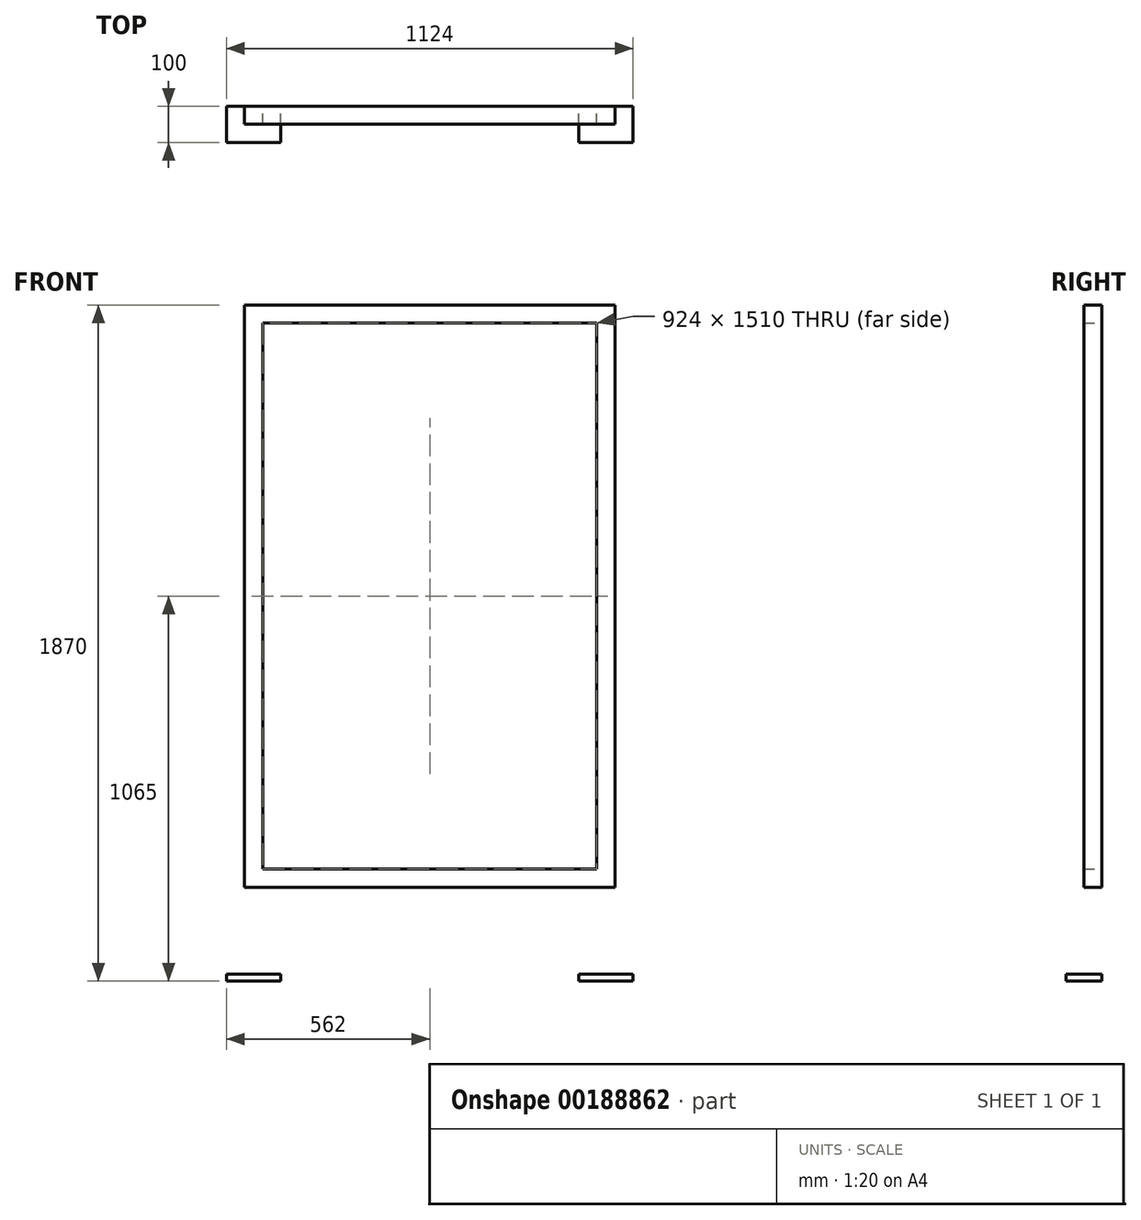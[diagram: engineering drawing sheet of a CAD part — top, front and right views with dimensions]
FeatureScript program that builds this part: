
annotation { "Feature Type Name" : "Feature", "Feature Type Description" : "" }
export const myFeature = defineFeature(function(context is Context, id is Id, definition is map)
    precondition{}
    {
        {
            var Q0;
            Q0=qCreatedBy(makeId("Front.planeOp"),FACE);
            var sketch = newSketch(context, id + "F0", { "sketchPlane" : qUnion([Q0])});
            skLineSegment(sketch, "E0.bottom", {"start": v(-1024, 0) * mm, "end": v(0, 0) * mm});
            skLineSegment(sketch, "E0.top", {"start": v(-1024, -1610) * mm, "end": v(0, -1610) * mm});
            skLineSegment(sketch, "E0.left", {"start": v(-1024, 0) * mm, "end": v(-1024, -1610) * mm});
            skLineSegment(sketch, "E0.right", {"start": v(0, 0) * mm, "end": v(0, -1610) * mm});
            skLineSegment(sketch, "E1.bottom", {"start": v(-974, -50) * mm, "end": v(-50, -50) * mm});
            skLineSegment(sketch, "E1.top", {"start": v(-974, -1560) * mm, "end": v(-50, -1560) * mm});
            skLineSegment(sketch, "E1.left", {"start": v(-974, -50) * mm, "end": v(-974, -1560) * mm});
            skLineSegment(sketch, "E1.right", {"start": v(-50, -50) * mm, "end": v(-50, -1560) * mm});
            skLineSegment(sketch, "E2.bottom", {"start": v(-1024, -1610) * mm, "end": v(-974, -1610) * mm});
            skLineSegment(sketch, "E2.top", {"start": v(-1024, -1850) * mm, "end": v(-974, -1850) * mm});
            skLineSegment(sketch, "E2.left", {"start": v(-1024, -1610) * mm, "end": v(-1024, -1850) * mm});
            skLineSegment(sketch, "E2.right", {"start": v(-974, -1610) * mm, "end": v(-974, -1850) * mm});
            skLineSegment(sketch, "E3.bottom", {"start": v(0, -1610) * mm, "end": v(-50, -1610) * mm});
            skLineSegment(sketch, "E3.top", {"start": v(0, -1850) * mm, "end": v(-50, -1850) * mm});
            skLineSegment(sketch, "E3.left", {"start": v(0, -1610) * mm, "end": v(0, -1850) * mm});
            skLineSegment(sketch, "E3.right", {"start": v(-50, -1610) * mm, "end": v(-50, -1850) * mm});
            skLineSegment(sketch, "E4.bottom", {"start": v(-1074, -1850) * mm, "end": v(-924, -1850) * mm});
            skLineSegment(sketch, "E4.top", {"start": v(-1074, -1870) * mm, "end": v(-924, -1870) * mm});
            skLineSegment(sketch, "E4.left", {"start": v(-1074, -1850) * mm, "end": v(-1074, -1870) * mm});
            skLineSegment(sketch, "E4.right", {"start": v(-924, -1850) * mm, "end": v(-924, -1870) * mm});
            skLineSegment(sketch, "E5.bottom", {"start": v(-100, -1850) * mm, "end": v(50, -1850) * mm});
            skLineSegment(sketch, "E5.top", {"start": v(-100, -1870) * mm, "end": v(50, -1870) * mm});
            skLineSegment(sketch, "E5.left", {"start": v(-100, -1850) * mm, "end": v(-100, -1870) * mm});
            skLineSegment(sketch, "E5.right", {"start": v(50, -1850) * mm, "end": v(50, -1870) * mm});
            skSolve(sketch);
        }
        {
            var Q0;
            Q0=makeQuery(id+"F0.imprint","IMPRINT",FACE,{"disambiguationData":[TD([[makeQuery(id+"F0.imprint","IMPRINT",EDGE,{"derivedFrom":sQuery(id+"F0.wireOp",EDGE,"E0.bottom")}),-1.0]])]});
            var Q1;
            Q1=makeQuery(id+"F0.imprint","IMPRINT",FACE,{"disambiguationData":[TD([[makeQuery(id+"F0.imprint","IMPRINT",EDGE,{"derivedFrom":sQuery(id+"F0.wireOp",EDGE,"E2.bottom")}),-1.0]])]});
            var Q2;
            Q2=makeQuery(id+"F0.imprint","IMPRINT",FACE,{"disambiguationData":[TD([[makeQuery(id+"F0.imprint","IMPRINT",EDGE,{"derivedFrom":sQuery(id+"F0.wireOp",EDGE,"E3.bottom")}),1.0]])]});
            extrude(context, id + "F1", {"entities" : qUnion([Q0, Q1, Q2]), "depth" : 50 * mm});
        }
        {
            var Q0;
            Q0=makeQuery(id+"F0.imprint","IMPRINT",FACE,{"disambiguationData":[TD([[makeQuery(id+"F0.imprint","IMPRINT",EDGE,{"derivedFrom":sQuery(id+"F0.wireOp",EDGE,"E4.top")}),1.0]])]});
            extrude(context, id + "F2", {"entities" : qUnion([Q0]), "operationType" : NewBodyOperationType.ADD, "depth" : 100 * mm});
        }
        {
            var Q0;
            Q0=makeQuery(id+"F0.imprint","IMPRINT",FACE,{"disambiguationData":[TD([[makeQuery(id+"F0.imprint","IMPRINT",EDGE,{"derivedFrom":sQuery(id+"F0.wireOp",EDGE,"E5.top")}),1.0]])]});
            extrude(context, id + "F3", {"entities" : qUnion([Q0]), "operationType" : NewBodyOperationType.ADD, "depth" : 100 * mm});
        }
    });
